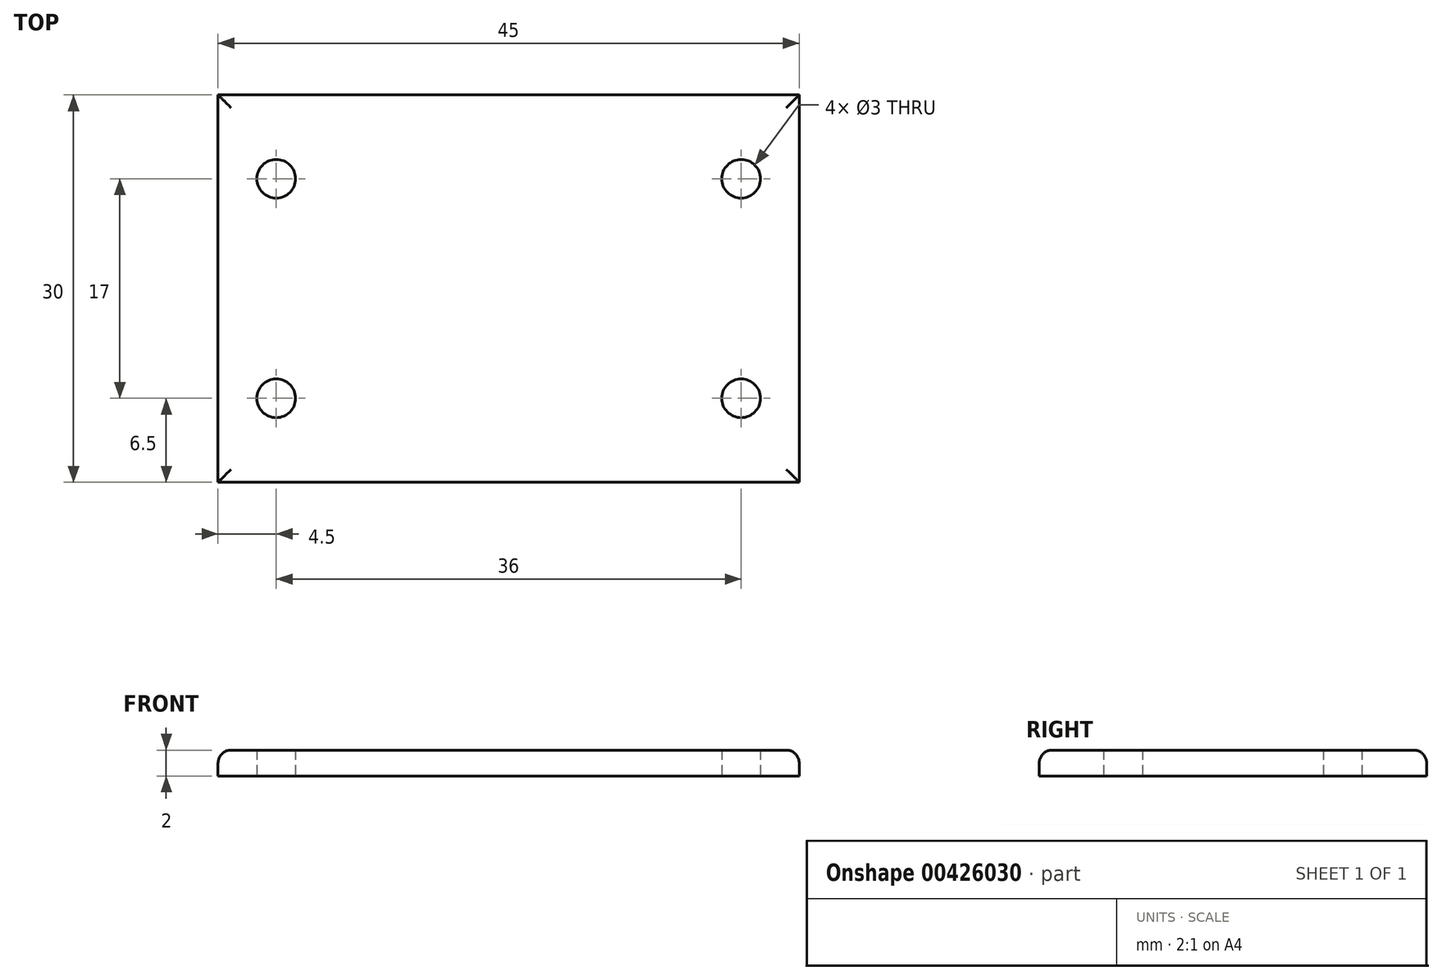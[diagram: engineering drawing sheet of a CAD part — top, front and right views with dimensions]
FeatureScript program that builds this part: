
annotation { "Feature Type Name" : "Feature", "Feature Type Description" : "" }
export const myFeature = defineFeature(function(context is Context, id is Id, definition is map)
    precondition{}
    {
        {
            var Q0;
            Q0=qCreatedBy(makeId("Top.planeOp"),FACE);
            var sketch = newSketch(context, id + "F0", { "sketchPlane" : qUnion([Q0])});
            skLineSegment(sketch, "E0.bottom", {"start": v(22.5, -15) * mm, "end": v(-22.5, -15) * mm});
            skLineSegment(sketch, "E0.top", {"start": v(22.5, 15) * mm, "end": v(-22.5, 15) * mm});
            skLineSegment(sketch, "E0.left", {"start": v(22.5, -15) * mm, "end": v(22.5, 15) * mm});
            skLineSegment(sketch, "E0.right", {"start": v(-22.5, -15) * mm, "end": v(-22.5, 15) * mm});
            skPoint(sketch, "E0.middle", {"position": v(0, 0) * mm});
            skLineSegment(sketch, "E1", {"start": v(0, 40.09) * mm, "end": v(0, -36.39) * mm, "construction": true});
            skCircle(sketch, "E2", {"center": v(-18, 8.5) * mm, "radius": 1.5 * mm});
            skCircle(sketch, "E3.MirrorC", {"center": v(18, 8.5) * mm, "radius": 1.5 * mm});
            skCircle(sketch, "E4.MirrorC", {"center": v(-18, -8.5) * mm, "radius": 1.5 * mm});
            skCircle(sketch, "E5.MirrorC", {"center": v(18, -8.5) * mm, "radius": 1.5 * mm});
            skSolve(sketch);
        }
        {
            var Q0;
            Q0=makeQuery(id+"F0.imprint","IMPRINT",FACE,{"disambiguationData":[TD([[makeQuery(id+"F0.imprint","IMPRINT",EDGE,{"derivedFrom":sQuery(id+"F0.wireOp",EDGE,"E0.bottom")}),-1.0]])]});
            extrude(context, id + "F1", {"entities" : qUnion([Q0]), "depth" : 2 * mm, "offsetDistance" : 25 * mm});
        }
        {
            var Q0;
            Q0=makeQuery(id+"F1.opExtrude","CAP_EDGE",EDGE,{"disambiguationData":[OSD([sQuery(id+"F0.wireOp",EDGE,"E0.right")])],"isStart":false});
            var Q1;
            Q1=makeQuery(id+"F1.opExtrude","CAP_EDGE",EDGE,{"disambiguationData":[OSD([sQuery(id+"F0.wireOp",EDGE,"E0.top")])],"isStart":false});
            var Q2;
            Q2=makeQuery(id+"F1.opExtrude","CAP_EDGE",EDGE,{"disambiguationData":[OSD([sQuery(id+"F0.wireOp",EDGE,"E0.left")])],"isStart":false});
            var Q3;
            Q3=makeQuery(id+"F1.opExtrude","CAP_EDGE",EDGE,{"disambiguationData":[OSD([sQuery(id+"F0.wireOp",EDGE,"E0.bottom")])],"isStart":false});
            fillet(context, id + "F2", {"entities" : qUnion([Q0, Q1, Q2, Q3]), "radius" : 1 * mm, "tangentPropagation" : true, "allowEdgeOverflow" : false});
        }
    });
